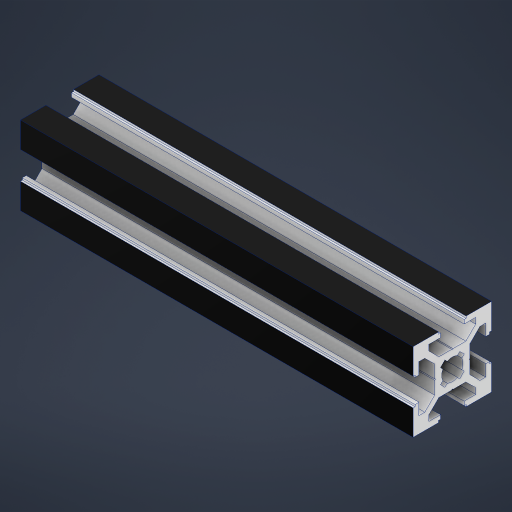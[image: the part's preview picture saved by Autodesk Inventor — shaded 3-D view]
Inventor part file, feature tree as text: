
AUTODESK INVENTOR PART (.ipt)
format: ipt  version: 2024.2 (Build 282272000, 272)  size: 354,304 bytes
history: native  units: mm
features: extrude x1, sketch x1
ambient origin geometry x8: Origin, YZ Plane, XZ Plane, XY Plane, X Axis, Y Axis, Z Axis, Center Point
bodies: Solid1 (feature_tree)
feature tree (2):
  extrude  "Extrusion1"  Depth=0.5mm
  sketch  "Sketch1"  dims[d2=6.5mm d3=0.5mm d4=4.0mm d5=3.465mm d6=5.48mm d7=0.795mm d8=0.305mm d9=2.95mm d11=0.75mm d14=45.0deg d15=10.0mm d16=1.0mm d17=3.0mm d18=45.0deg d19=40.0mm d21=360.0deg d23=100.0mm d24=0.0mm]
